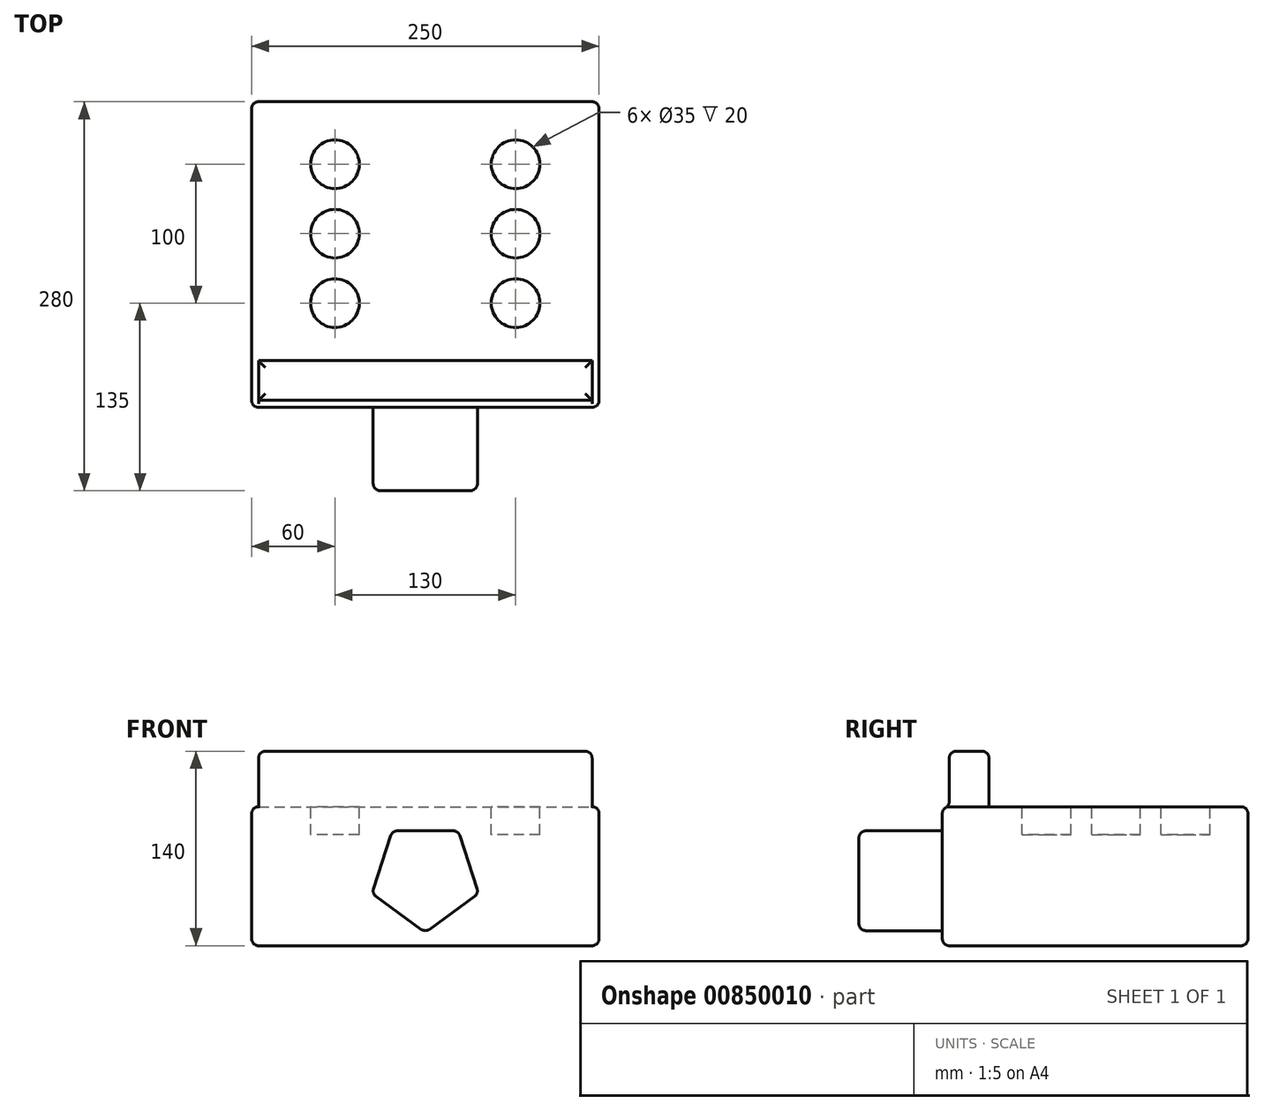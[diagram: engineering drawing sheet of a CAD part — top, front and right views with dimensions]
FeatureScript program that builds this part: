
annotation { "Feature Type Name" : "Feature", "Feature Type Description" : "" }
export const myFeature = defineFeature(function(context is Context, id is Id, definition is map)
    precondition{}
    {
        {
            var Q0;
            Q0=qCreatedBy(makeId("Front.planeOp"),FACE);
            var sketch = newSketch(context, id + "F0", { "sketchPlane" : qUnion([Q0])});
            skLineSegment(sketch, "E0.bottom", {"start": v(125, -50) * mm, "end": v(-125, -50) * mm});
            skLineSegment(sketch, "E0.top", {"start": v(125, 50) * mm, "end": v(-125, 50) * mm});
            skLineSegment(sketch, "E0.left", {"start": v(125, -50) * mm, "end": v(125, 50) * mm});
            skLineSegment(sketch, "E0.right", {"start": v(-125, -50) * mm, "end": v(-125, 50) * mm});
            skPoint(sketch, "E0.middle", {"position": v(0, 0) * mm});
            skSolve(sketch);
        }
        {
            var Q0;
            Q0=makeQuery(id+"F0.imprint","IMPRINT",FACE,{"disambiguationData":[TD([[makeQuery(id+"F0.imprint","IMPRINT",EDGE,{"derivedFrom":sQuery(id+"F0.wireOp",EDGE,"E0.bottom")}),-1.0]])]});
            extrude(context, id + "F1", {"entities" : qUnion([Q0]), "depth" : 220 * mm, "offsetDistance" : 25 * mm});
        }
        {
            var Q0;
            Q0=makeQuery(id+"F1.opExtrude","SWEPT_FACE",FACE,{"disambiguationData":[OSD([sQuery(id+"F0.wireOp",EDGE,"E0.top")])]});
            var Q1;
            Q1=makeQuery(id+"F1.opExtrude","SWEPT_FACE",FACE,{"disambiguationData":[OSD([sQuery(id+"F0.wireOp",EDGE,"E0.bottom")])]});
            var Q2;
            Q2=makeQuery(id+"F1.opExtrude","CAP_EDGE",EDGE,{"disambiguationData":[OSD([sQuery(id+"F0.wireOp",EDGE,"E0.left")])],"isStart":false});
            var Q3;
            Q3=makeQuery(id+"F1.opExtrude","CAP_EDGE",EDGE,{"disambiguationData":[OSD([sQuery(id+"F0.wireOp",EDGE,"E0.right")])],"isStart":false});
            var Q4;
            Q4=makeQuery(id+"F1.opExtrude","CAP_EDGE",EDGE,{"disambiguationData":[OSD([sQuery(id+"F0.wireOp",EDGE,"E0.right")])],"isStart":true});
            var Q5;
            Q5=makeQuery(id+"F1.opExtrude","CAP_EDGE",EDGE,{"disambiguationData":[OSD([sQuery(id+"F0.wireOp",EDGE,"E0.left")])],"isStart":true});
            fillet(context, id + "F2", {"entities" : qUnion([Q0, Q1, Q2, Q3, Q4, Q5]), "radius" : 5 * mm, "tangentPropagation" : true, "allowEdgeOverflow" : false});
        }
        {
            var Q0;
            Q0=makeQuery(id+"F1.opExtrude","CAP_FACE",FACE,{"disambiguationData":[OSD([sQuery(id+"F0.wireOp",EDGE,"E0.bottom"),sQuery(id+"F0.wireOp",EDGE,"E0.top"),sQuery(id+"F0.wireOp",EDGE,"E0.left"),sQuery(id+"F0.wireOp",EDGE,"E0.right")])],"isStart":false});
            var sketch = newSketch(context, id + "F3", { "sketchPlane" : qUnion([Q0])});
            skCircle(sketch, "E1.cCircle", {"center": v(0, 0) * mm, "radius": 32.65 * mm, "construction": true});
            skPoint(sketch, "E1.cCircle.perimeterSnap0", {"position": v(0, 45) * mm});
            skLineSegment(sketch, "E1.0", {"start": v(-23.72, 32.65) * mm, "end": v(23.72, 32.65) * mm});
            skLineSegment(sketch, "E1.1", {"start": v(23.72, 32.65) * mm, "end": v(38.38, -12.47) * mm});
            skLineSegment(sketch, "E1.2", {"start": v(38.38, -12.47) * mm, "end": v(0, -40.36) * mm});
            skLineSegment(sketch, "E1.3", {"start": v(0, -40.36) * mm, "end": v(-38.38, -12.47) * mm});
            skLineSegment(sketch, "E1.4", {"start": v(-38.38, -12.47) * mm, "end": v(-23.72, 32.65) * mm});
            skPoint(sketch, "E1.0.midPoint", {"position": v(0, 32.65) * mm});
            skPoint(sketch, "E1.0.midPoint.positionSnap0", {"position": v(0, 45) * mm});
            skSolve(sketch);
        }
        {
            var Q0;
            Q0=makeQuery(id+"F3.imprint","IMPRINT",FACE,{"disambiguationData":[TD([[makeQuery(id+"F3.imprint","IMPRINT",EDGE,{"derivedFrom":sQuery(id+"F3.wireOp",EDGE,"E1.0")}),-1.0]])]});
            extrude(context, id + "F4", {"entities" : qUnion([Q0]), "operationType" : NewBodyOperationType.ADD, "depth" : 60 * mm, "offsetDistance" : 25 * mm});
        }
        {
            var Q0;
            Q0=makeQuery(id+"F1.opExtrude","SWEPT_FACE",FACE,{"disambiguationData":[OSD([sQuery(id+"F0.wireOp",EDGE,"E0.top")])]});
            var sketch = newSketch(context, id + "F5", { "sketchPlane" : qUnion([Q0])});
            skLineSegment(sketch, "E2", {"start": v(-120, -186.41) * mm, "end": v(120, -186.41) * mm});
            skSolve(sketch);
        }
        {
            var Q0;
            {var subQ0=sQuery(id+"F5.wireOp",EDGE,"E2");Q0=makeQuery(id+"F5.imprint","IMPRINT",FACE,{"disambiguationData":[TD([[makeQuery(id+"F5.imprint","IMPRINT",EDGE,{"derivedFrom":subQ0}),-1.0]])]});}
            extrude(context, id + "F6", {"entities" : qUnion([Q0]), "operationType" : NewBodyOperationType.ADD, "depth" : 40 * mm, "offsetDistance" : 25 * mm});
        }
        {
            var Q0;
            Q0=makeQuery(id+"F6.opExtrude","CAP_FACE",FACE,{"disambiguationData":[OSD([sQuery(id+"F0.wireOp",EDGE,"E0.top"),sQuery(id+"F0.wireOp",EDGE,"E0.left"),sQuery(id+"F0.wireOp",EDGE,"E0.right"),sQuery(id+"F5.wireOp",EDGE,"E2")])],"isStart":false});
            var Q1;
            {var subQ0=sQuery(id+"F0.wireOp",EDGE,"E0.top");Q1=makeQuery(id+"F6.boolean.opBoolean","MERGE",EDGE,{"derivedFrom":[makeQuery(id+"F2.opFillet","BLEND_EDGE",EDGE,{"blendedFrom":[makeQuery(id+"F1.opExtrude","CAP_EDGE",EDGE,{"disambiguationData":[OSD([subQ0])],"isStart":false}),makeQuery(id+"F1.opExtrude","SWEPT_FACE",FACE,{"disambiguationData":[OSD([subQ0])]})],"blendedInto":[makeQuery(id+"F1.opExtrude","SWEPT_FACE",FACE,{"disambiguationData":[OSD([subQ0])]})]}),makeQuery(id+"F6.opExtrude","CAP_EDGE",EDGE,{"disambiguationData":[OSD([subQ0])],"isStart":true})]});}
            var Q2;
            Q2=makeQuery(id+"F6.opExtrude","CAP_EDGE",EDGE,{"disambiguationData":[OSD([sQuery(id+"F0.wireOp",EDGE,"E0.top")])],"isStart":false});
            fillet(context, id + "F7", {"entities" : qUnion([Q0, Q1, Q2]), "radius" : 5 * mm, "tangentPropagation" : true, "allowEdgeOverflow" : false});
        }
        {
            var Q0;
            Q0=makeQuery(id+"F4.opExtrude","CAP_EDGE",EDGE,{"disambiguationData":[OSD([sQuery(id+"F3.wireOp",EDGE,"E1.0")])],"isStart":true});
            var Q1;
            Q1=makeQuery(id+"F4.opExtrude","CAP_EDGE",EDGE,{"disambiguationData":[OSD([sQuery(id+"F3.wireOp",EDGE,"E1.1")])],"isStart":true});
            var Q2;
            Q2=makeQuery(id+"F4.opExtrude","CAP_EDGE",EDGE,{"disambiguationData":[OSD([sQuery(id+"F3.wireOp",EDGE,"E1.2")])],"isStart":true});
            var Q3;
            Q3=makeQuery(id+"F4.opExtrude","CAP_EDGE",EDGE,{"disambiguationData":[OSD([sQuery(id+"F3.wireOp",EDGE,"E1.3")])],"isStart":true});
            var Q4;
            Q4=makeQuery(id+"F4.opExtrude","CAP_EDGE",EDGE,{"disambiguationData":[OSD([sQuery(id+"F3.wireOp",EDGE,"E1.4")])],"isStart":true});
            var Q5;
            Q5=makeQuery(id+"F4.opExtrude","CAP_FACE",FACE,{"disambiguationData":[OSD([sQuery(id+"F3.wireOp",EDGE,"E1.0"),sQuery(id+"F3.wireOp",EDGE,"E1.1"),sQuery(id+"F3.wireOp",EDGE,"E1.2"),sQuery(id+"F3.wireOp",EDGE,"E1.3"),sQuery(id+"F3.wireOp",EDGE,"E1.4")])],"isStart":false});
            var Q6;
            Q6=makeQuery(id+"F4.opExtrude","SWEPT_EDGE",EDGE,{"disambiguationData":[OSD([sQuery(id+"F3.wireOp",EDGE,"E1.0"),sQuery(id+"F3.wireOp",EDGE,"E1.4")])]});
            var Q7;
            Q7=makeQuery(id+"F4.opExtrude","SWEPT_EDGE",EDGE,{"disambiguationData":[OSD([sQuery(id+"F3.wireOp",EDGE,"E1.0"),sQuery(id+"F3.wireOp",EDGE,"E1.1")])]});
            var Q8;
            Q8=makeQuery(id+"F4.opExtrude","SWEPT_EDGE",EDGE,{"disambiguationData":[OSD([sQuery(id+"F3.wireOp",EDGE,"E1.1"),sQuery(id+"F3.wireOp",EDGE,"E1.2")])]});
            var Q9;
            Q9=makeQuery(id+"F4.opExtrude","SWEPT_EDGE",EDGE,{"disambiguationData":[OSD([sQuery(id+"F3.wireOp",EDGE,"E1.2"),sQuery(id+"F3.wireOp",EDGE,"E1.3")])]});
            var Q10;
            Q10=makeQuery(id+"F4.opExtrude","SWEPT_EDGE",EDGE,{"disambiguationData":[OSD([sQuery(id+"F3.wireOp",EDGE,"E1.3"),sQuery(id+"F3.wireOp",EDGE,"E1.4")])]});
            fillet(context, id + "F8", {"entities" : qUnion([Q0, Q1, Q2, Q3, Q4, Q5, Q6, Q7, Q8, Q9, Q10]), "radius" : 5 * mm, "tangentPropagation" : true, "allowEdgeOverflow" : false});
        }
        {
            var Q0;
            Q0=makeQuery(id+"F1.opExtrude","SWEPT_FACE",FACE,{"disambiguationData":[OSD([sQuery(id+"F0.wireOp",EDGE,"E0.top")])]});
            var sketch = newSketch(context, id + "F9", { "sketchPlane" : qUnion([Q0])});
            skCircle(sketch, "E3", {"center": v(65, -45) * mm, "radius": 17.5 * mm});
            skCircle(sketch, "E4", {"center": v(-65, -45) * mm, "radius": 17.5 * mm});
            skCircle(sketch, "E5.0.1.0", {"center": v(-65, -95) * mm, "radius": 17.5 * mm});
            skCircle(sketch, "E5.0.2.0", {"center": v(-65, -145) * mm, "radius": 17.5 * mm});
            skLineSegment(sketch, "E5.direction1", {"start": v(-65, -45) * mm, "end": v(31, -45) * mm, "construction": true});
            skLineSegment(sketch, "E5.direction2", {"start": v(-65, -45) * mm, "end": v(-65, -95) * mm, "construction": true});
            skCircle(sketch, "E6.0.1.0", {"center": v(65, -95) * mm, "radius": 17.5 * mm});
            skCircle(sketch, "E6.0.2.0", {"center": v(65, -145) * mm, "radius": 17.5 * mm});
            skLineSegment(sketch, "E6.direction1", {"start": v(65, -45) * mm, "end": v(90, -45) * mm, "construction": true});
            skLineSegment(sketch, "E6.direction2", {"start": v(65, -45) * mm, "end": v(65, -95) * mm, "construction": true});
            skSolve(sketch);
        }
        {
            var Q0;
            Q0=makeQuery(id+"F9.imprint","IMPRINT",FACE,{"disambiguationData":[TD([[makeQuery(id+"F9.imprint","IMPRINT",EDGE,{"derivedFrom":sQuery(id+"F9.wireOp",EDGE,"E4")}),1.0]])]});
            var Q1;
            Q1=makeQuery(id+"F9.imprint","IMPRINT",FACE,{"disambiguationData":[TD([[makeQuery(id+"F9.imprint","IMPRINT",EDGE,{"derivedFrom":sQuery(id+"F9.wireOp",EDGE,"E5.0.1.0")}),1.0]])]});
            var Q2;
            Q2=makeQuery(id+"F9.imprint","IMPRINT",FACE,{"disambiguationData":[TD([[makeQuery(id+"F9.imprint","IMPRINT",EDGE,{"derivedFrom":sQuery(id+"F9.wireOp",EDGE,"E5.0.2.0")}),1.0]])]});
            var Q3;
            Q3=makeQuery(id+"F9.imprint","IMPRINT",FACE,{"disambiguationData":[TD([[makeQuery(id+"F9.imprint","IMPRINT",EDGE,{"derivedFrom":sQuery(id+"F9.wireOp",EDGE,"E6.0.2.0")}),1.0]])]});
            var Q4;
            Q4=makeQuery(id+"F9.imprint","IMPRINT",FACE,{"disambiguationData":[TD([[makeQuery(id+"F9.imprint","IMPRINT",EDGE,{"derivedFrom":sQuery(id+"F9.wireOp",EDGE,"E6.0.1.0")}),1.0]])]});
            var Q5;
            Q5=makeQuery(id+"F9.imprint","IMPRINT",FACE,{"disambiguationData":[TD([[makeQuery(id+"F9.imprint","IMPRINT",EDGE,{"derivedFrom":sQuery(id+"F9.wireOp",EDGE,"E3")}),1.0]])]});
            extrude(context, id + "F10", {"entities" : qUnion([Q0, Q1, Q2, Q3, Q4, Q5]), "operationType" : NewBodyOperationType.REMOVE, "oppositeDirection" : true, "depth" : 20 * mm, "offsetDistance" : 25 * mm});
        }
    });
